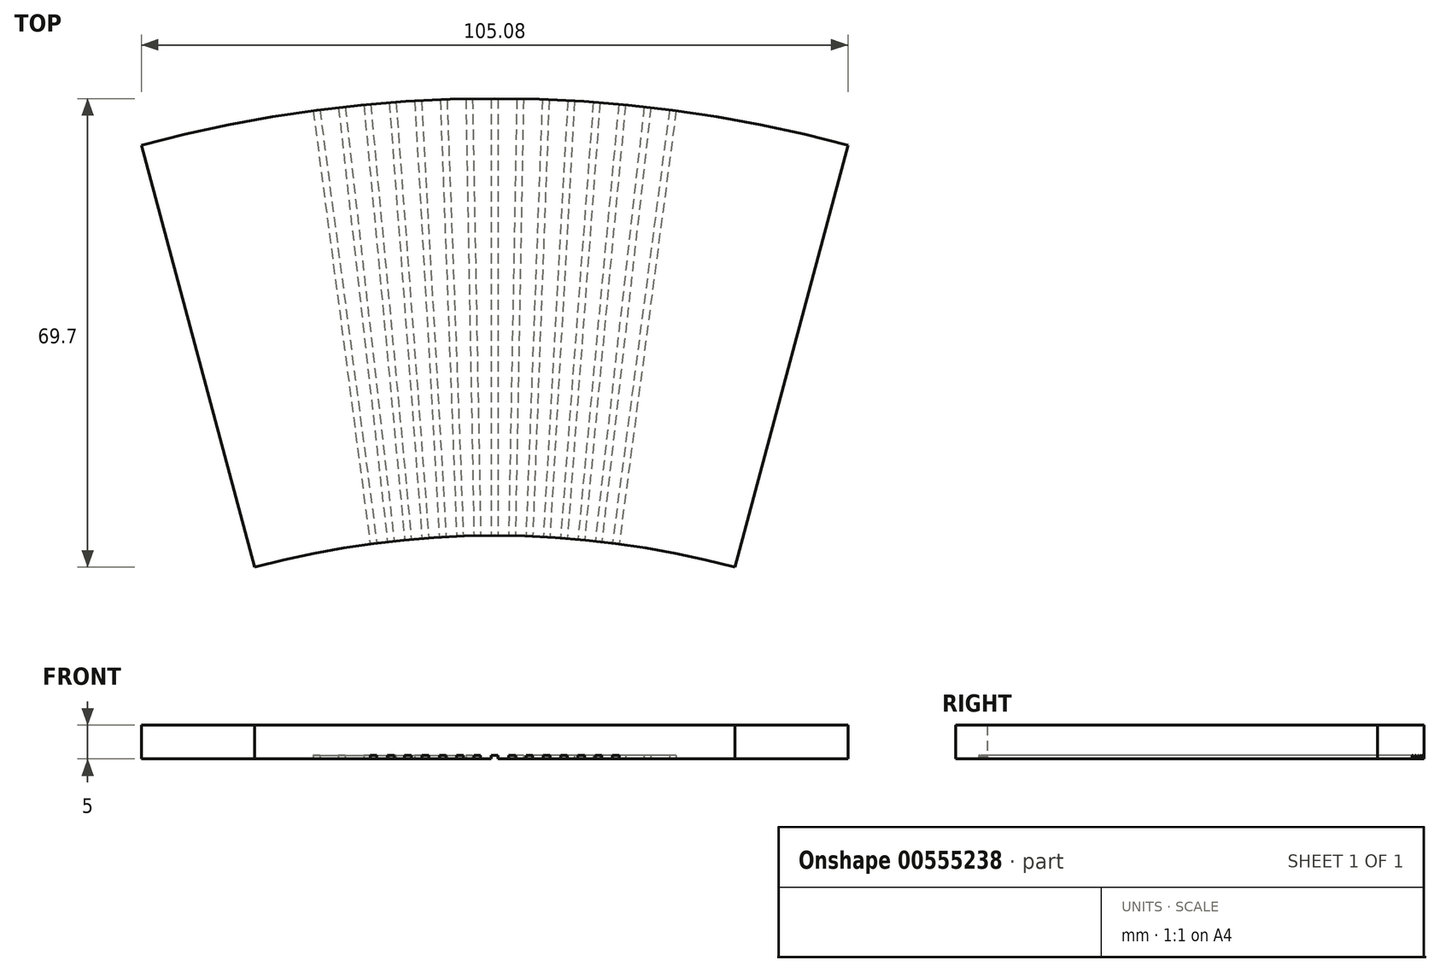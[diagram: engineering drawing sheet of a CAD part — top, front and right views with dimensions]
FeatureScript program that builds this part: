
annotation { "Feature Type Name" : "Feature", "Feature Type Description" : "" }
export const myFeature = defineFeature(function(context is Context, id is Id, definition is map)
    precondition{}
    {
        {
            var Q0;
            Q0=qCreatedBy(makeId("Right.planeOp"),FACE);
            var sketch = newSketch(context, id + "F0", { "sketchPlane" : qUnion([Q0])});
            skLineSegment(sketch, "E0", {"start": v(0, 0) * mm, "end": v(0, 5) * mm});
            skLineSegment(sketch, "E1", {"start": v(0, 5) * mm, "end": v(65, 5) * mm});
            skLineSegment(sketch, "E2", {"start": v(65, 5) * mm, "end": v(65, 0) * mm});
            skLineSegment(sketch, "E3", {"start": v(65, 0) * mm, "end": v(0, 0) * mm});
            skLineSegment(sketch, "E4", {"start": v(-138, 0) * mm, "end": v(-138, 30.85) * mm});
            skSolve(sketch);
        }
        {
            var Q0;
            Q0=makeQuery(id+"F0.imprint","IMPRINT",FACE,{"disambiguationData":[TD([[makeQuery(id+"F0.imprint","IMPRINT",EDGE,{"derivedFrom":sQuery(id+"F0.wireOp",EDGE,"E0")}),-1.0]])]});
            var Q1;
            Q1=sQuery(id+"F0.wireOp",EDGE,"E4");
            revolve(context, id + "F1", {"entities" : qUnion([Q0]), "axis" : qUnion([Q1]), "revolveType" : RevolveType.SYMMETRIC, "angle" : 30 * degree});
        }
        {
            var Q0;
            Q0=qCreatedBy(makeId("Top.planeOp"),FACE);
            var sketch = newSketch(context, id + "F2", { "sketchPlane" : qUnion([Q0])});
            skLineSegment(sketch, "E5", {"start": v(0, -138) * mm, "end": v(-26.5, 63.26) * mm});
            skLineSegment(sketch, "E6", {"start": v(0, -138) * mm, "end": v(26.5, 63.26) * mm});
            skLineSegment(sketch, "E7.1.0", {"start": v(0, -138) * mm, "end": v(-22.73, 63.72) * mm});
            skLineSegment(sketch, "E7.2.0", {"start": v(0, -138) * mm, "end": v(-18.95, 64.11) * mm});
            skLineSegment(sketch, "E7.3.0", {"start": v(0, -138) * mm, "end": v(-15.17, 64.43) * mm});
            skLineSegment(sketch, "E7.4.0", {"start": v(0, -138) * mm, "end": v(-11.38, 64.68) * mm});
            skLineSegment(sketch, "E7.5.0", {"start": v(0, -138) * mm, "end": v(-7.6, 64.86) * mm});
            skLineSegment(sketch, "E7.6.0", {"start": v(0, -138) * mm, "end": v(-3.8, 64.96) * mm});
            skLineSegment(sketch, "E7.7.0", {"start": v(0, -138) * mm, "end": v(0, 65) * mm});
            skLineSegment(sketch, "E7.8.0", {"start": v(0, -138) * mm, "end": v(3.8, 64.96) * mm});
            skLineSegment(sketch, "E7.9.0", {"start": v(0, -138) * mm, "end": v(7.6, 64.86) * mm});
            skLineSegment(sketch, "E7.10.0", {"start": v(0, -138) * mm, "end": v(11.38, 64.68) * mm});
            skLineSegment(sketch, "E7.11.0", {"start": v(0, -138) * mm, "end": v(15.17, 64.43) * mm});
            skLineSegment(sketch, "E7.12.0", {"start": v(0, -138) * mm, "end": v(18.95, 64.11) * mm});
            skLineSegment(sketch, "E7.13.0", {"start": v(0, -138) * mm, "end": v(22.73, 63.72) * mm});
            skPoint(sketch, "E7.center", {"position": v(0, -138) * mm});
            skLineSegment(sketch, "E7.anchor1", {"start": v(0, -138) * mm, "end": v(-26.5, 63.26) * mm, "construction": true});
            skLineSegment(sketch, "E7.anchor2", {"start": v(0, -138) * mm, "end": v(26.5, 63.26) * mm, "construction": true});
            skLineSegment(sketch, "E8.bottom", {"start": v(43.3, 187.13) * mm, "end": v(42.32, 187.26) * mm});
            skLineSegment(sketch, "E8.top", {"start": v(10.68, -60.73) * mm, "end": v(9.69, -60.6) * mm});
            skLineSegment(sketch, "E8.left", {"start": v(43.3, 187.13) * mm, "end": v(10.68, -60.73) * mm});
            skLineSegment(sketch, "E8.right", {"start": v(42.32, 187.26) * mm, "end": v(9.69, -60.6) * mm});
            skPoint(sketch, "E8.middle", {"position": v(26.5, 63.26) * mm});
            skLineSegment(sketch, "E9.bottom", {"start": v(37.22, 187.88) * mm, "end": v(36.23, 188) * mm});
            skLineSegment(sketch, "E9.top", {"start": v(9.23, -60.55) * mm, "end": v(8.24, -60.43) * mm});
            skLineSegment(sketch, "E9.left", {"start": v(37.22, 187.88) * mm, "end": v(9.23, -60.55) * mm});
            skLineSegment(sketch, "E9.right", {"start": v(36.23, 188) * mm, "end": v(8.24, -60.43) * mm});
            skPoint(sketch, "E9.middle", {"position": v(22.73, 63.72) * mm});
            skLineSegment(sketch, "E10.bottom", {"start": v(31.12, 188.52) * mm, "end": v(30.13, 188.61) * mm});
            skLineSegment(sketch, "E10.top", {"start": v(7.78, -60.39) * mm, "end": v(6.78, -60.3) * mm});
            skLineSegment(sketch, "E10.left", {"start": v(31.12, 188.52) * mm, "end": v(7.78, -60.39) * mm});
            skLineSegment(sketch, "E10.right", {"start": v(30.13, 188.61) * mm, "end": v(6.78, -60.3) * mm});
            skPoint(sketch, "E10.middle", {"position": v(18.95, 64.11) * mm});
            skLineSegment(sketch, "E11.bottom", {"start": v(25.01, 189.05) * mm, "end": v(24.01, 189.12) * mm});
            skLineSegment(sketch, "E11.top", {"start": v(6.33, -60.26) * mm, "end": v(5.33, -60.18) * mm});
            skLineSegment(sketch, "E11.left", {"start": v(25.01, 189.05) * mm, "end": v(6.33, -60.26) * mm});
            skLineSegment(sketch, "E11.right", {"start": v(24.01, 189.12) * mm, "end": v(5.33, -60.18) * mm});
            skPoint(sketch, "E11.middle", {"position": v(15.17, 64.43) * mm});
            skLineSegment(sketch, "E12.bottom", {"start": v(18.9, 189.46) * mm, "end": v(17.9, 189.51) * mm});
            skLineSegment(sketch, "E12.top", {"start": v(4.87, -60.15) * mm, "end": v(3.87, -60.1) * mm});
            skLineSegment(sketch, "E12.left", {"start": v(18.9, 189.46) * mm, "end": v(4.87, -60.15) * mm});
            skLineSegment(sketch, "E12.right", {"start": v(17.9, 189.51) * mm, "end": v(3.87, -60.1) * mm});
            skPoint(sketch, "E12.middle", {"position": v(11.38, 64.68) * mm});
            skLineSegment(sketch, "E13.bottom", {"start": v(6.63, 189.93) * mm, "end": v(5.63, 189.95) * mm});
            skLineSegment(sketch, "E13.top", {"start": v(1.96, -60.02) * mm, "end": v(0.96, -60) * mm});
            skLineSegment(sketch, "E13.left", {"start": v(6.63, 189.93) * mm, "end": v(1.96, -60.02) * mm});
            skLineSegment(sketch, "E13.right", {"start": v(5.63, 189.95) * mm, "end": v(0.96, -60) * mm});
            skPoint(sketch, "E13.middle", {"position": v(3.8, 64.96) * mm});
            skLineSegment(sketch, "E14.bottom", {"start": v(0.5, 190) * mm, "end": v(-0.5, 190) * mm});
            skLineSegment(sketch, "E14.top", {"start": v(0.5, -60) * mm, "end": v(-0.5, -60) * mm});
            skLineSegment(sketch, "E14.left", {"start": v(0.5, 190) * mm, "end": v(0.5, -60) * mm});
            skLineSegment(sketch, "E14.right", {"start": v(-0.5, 190) * mm, "end": v(-0.5, -60) * mm});
            skPoint(sketch, "E14.middle", {"position": v(0, 65) * mm});
            skLineSegment(sketch, "E15.bottom", {"start": v(12.76, 189.75) * mm, "end": v(11.76, 189.79) * mm});
            skLineSegment(sketch, "E15.top", {"start": v(3.42, -60.07) * mm, "end": v(2.42, -60.04) * mm});
            skLineSegment(sketch, "E15.left", {"start": v(12.76, 189.75) * mm, "end": v(3.42, -60.07) * mm});
            skLineSegment(sketch, "E15.right", {"start": v(11.76, 189.79) * mm, "end": v(2.42, -60.04) * mm});
            skPoint(sketch, "E15.middle", {"position": v(7.6, 64.86) * mm});
            skLineSegment(sketch, "E16.bottom", {"start": v(-5.63, 189.95) * mm, "end": v(-6.63, 189.93) * mm});
            skLineSegment(sketch, "E16.top", {"start": v(-0.96, -60) * mm, "end": v(-1.96, -60.02) * mm});
            skLineSegment(sketch, "E16.left", {"start": v(-5.63, 189.95) * mm, "end": v(-0.96, -60) * mm});
            skLineSegment(sketch, "E16.right", {"start": v(-6.63, 189.93) * mm, "end": v(-1.96, -60.02) * mm});
            skPoint(sketch, "E16.middle", {"position": v(-3.8, 64.96) * mm});
            skLineSegment(sketch, "E17.bottom", {"start": v(-30.13, 188.61) * mm, "end": v(-31.12, 188.52) * mm});
            skLineSegment(sketch, "E17.top", {"start": v(-6.78, -60.3) * mm, "end": v(-7.78, -60.39) * mm});
            skLineSegment(sketch, "E17.left", {"start": v(-30.13, 188.61) * mm, "end": v(-6.78, -60.3) * mm});
            skLineSegment(sketch, "E17.right", {"start": v(-31.12, 188.52) * mm, "end": v(-7.78, -60.39) * mm});
            skPoint(sketch, "E17.middle", {"position": v(-18.95, 64.11) * mm});
            skLineSegment(sketch, "E18.bottom", {"start": v(-36.23, 188) * mm, "end": v(-37.22, 187.88) * mm});
            skLineSegment(sketch, "E18.top", {"start": v(-8.24, -60.43) * mm, "end": v(-9.23, -60.55) * mm});
            skLineSegment(sketch, "E18.left", {"start": v(-36.23, 188) * mm, "end": v(-8.24, -60.43) * mm});
            skLineSegment(sketch, "E18.right", {"start": v(-37.22, 187.88) * mm, "end": v(-9.23, -60.55) * mm});
            skPoint(sketch, "E18.middle", {"position": v(-22.73, 63.72) * mm});
            skLineSegment(sketch, "E19.bottom", {"start": v(-42.32, 187.26) * mm, "end": v(-43.3, 187.13) * mm});
            skLineSegment(sketch, "E19.top", {"start": v(-9.69, -60.6) * mm, "end": v(-10.68, -60.73) * mm});
            skLineSegment(sketch, "E19.left", {"start": v(-42.32, 187.26) * mm, "end": v(-9.69, -60.6) * mm});
            skLineSegment(sketch, "E19.right", {"start": v(-43.3, 187.13) * mm, "end": v(-10.68, -60.73) * mm});
            skPoint(sketch, "E19.middle", {"position": v(-26.5, 63.26) * mm});
            skLineSegment(sketch, "E20.bottom", {"start": v(-24.01, 189.12) * mm, "end": v(-25.01, 189.05) * mm});
            skLineSegment(sketch, "E20.top", {"start": v(-5.33, -60.18) * mm, "end": v(-6.33, -60.26) * mm});
            skLineSegment(sketch, "E20.left", {"start": v(-24.01, 189.12) * mm, "end": v(-5.33, -60.18) * mm});
            skLineSegment(sketch, "E20.right", {"start": v(-25.01, 189.05) * mm, "end": v(-6.33, -60.26) * mm});
            skPoint(sketch, "E20.middle", {"position": v(-15.17, 64.43) * mm});
            skLineSegment(sketch, "E21.bottom", {"start": v(-17.9, 189.51) * mm, "end": v(-18.9, 189.46) * mm});
            skLineSegment(sketch, "E21.top", {"start": v(-3.87, -60.1) * mm, "end": v(-4.87, -60.15) * mm});
            skLineSegment(sketch, "E21.left", {"start": v(-17.9, 189.51) * mm, "end": v(-3.87, -60.1) * mm});
            skLineSegment(sketch, "E21.right", {"start": v(-18.9, 189.46) * mm, "end": v(-4.87, -60.15) * mm});
            skPoint(sketch, "E21.middle", {"position": v(-11.38, 64.68) * mm});
            skLineSegment(sketch, "E22.bottom", {"start": v(-11.76, 189.79) * mm, "end": v(-12.76, 189.75) * mm});
            skLineSegment(sketch, "E22.top", {"start": v(-2.42, -60.04) * mm, "end": v(-3.42, -60.07) * mm});
            skLineSegment(sketch, "E22.left", {"start": v(-11.76, 189.79) * mm, "end": v(-2.42, -60.04) * mm});
            skLineSegment(sketch, "E22.right", {"start": v(-12.76, 189.75) * mm, "end": v(-3.42, -60.07) * mm});
            skPoint(sketch, "E22.middle", {"position": v(-7.6, 64.86) * mm});
            skSolve(sketch);
        }
        {
            var Q0;
            Q0 = qSketchRegion(id + "F2", true);
            extrude(context, id + "F3", {"entities" : qUnion([Q0]), "operationType" : NewBodyOperationType.REMOVE, "depth" : .5 * mm, "offsetDistance" : 25 * mm});
        }
    });
